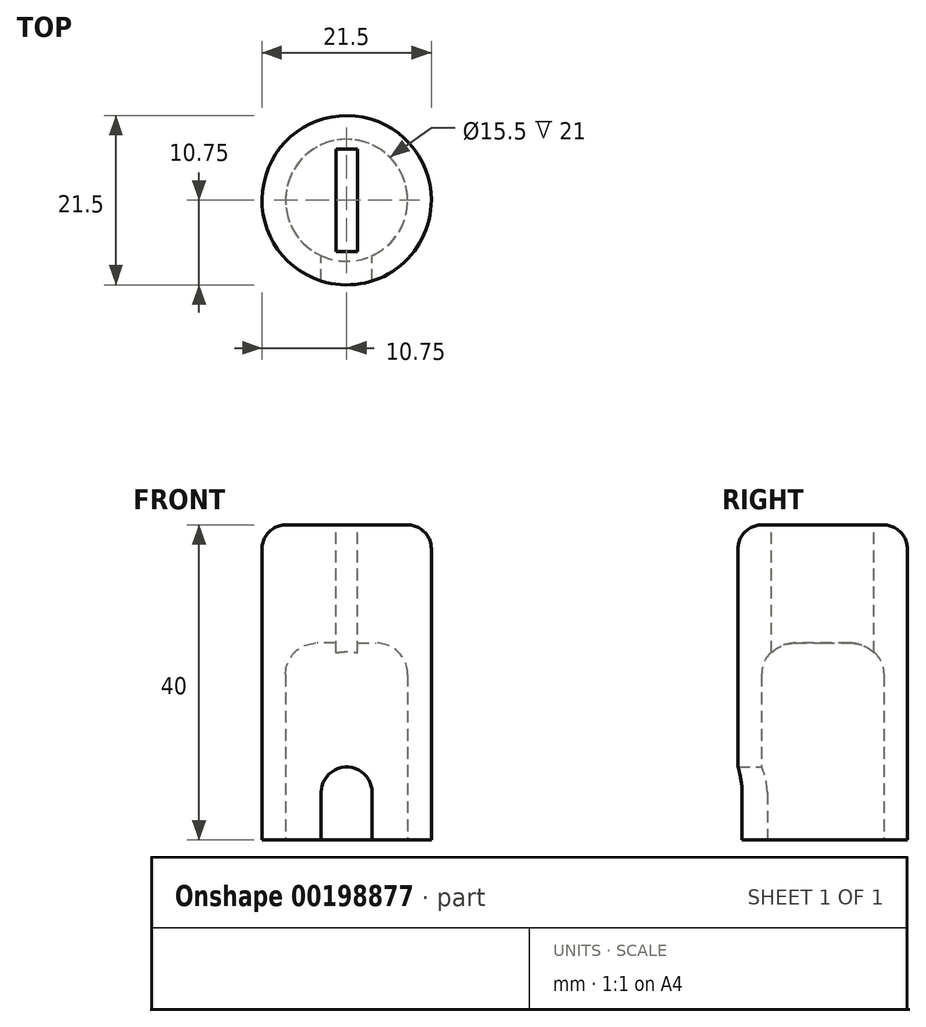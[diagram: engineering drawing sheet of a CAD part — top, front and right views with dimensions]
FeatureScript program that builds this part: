
annotation { "Feature Type Name" : "Feature", "Feature Type Description" : "" }
export const myFeature = defineFeature(function(context is Context, id is Id, definition is map)
    precondition{}
    {
        {
            var Q0;
            Q0=qCreatedBy(makeId("Top.planeOp"),FACE);
            var sketch = newSketch(context, id + "F0", { "sketchPlane" : qUnion([Q0])});
            skCircle(sketch, "E0", {"center": v(0, 0) * mm, "radius": 7.75 * mm});
            skCircle(sketch, "E1", {"center": v(0, 0) * mm, "radius": 10.75 * mm});
            skSolve(sketch);
        }
        {
            var Q0;
            Q0=makeQuery(id+"F0.imprint","IMPRINT",FACE,{"disambiguationData":[TD([[makeQuery(id+"F0.imprint","IMPRINT",EDGE,{"derivedFrom":sQuery(id+"F0.wireOp",EDGE,"E0")}),-1.0]])]});
            var Q1;
            Q1=makeQuery(id+"F0.imprint","IMPRINT",FACE,{"disambiguationData":[TD([[makeQuery(id+"F0.imprint","IMPRINT",EDGE,{"derivedFrom":sQuery(id+"F0.wireOp",EDGE,"E0")}),1.0]])]});
            extrude(context, id + "F1", {"entities" : qUnion([Q0, Q1]), "depth" : 40 * mm});
        }
        {
            var Q0;
            Q0=qCreatedBy(makeId("Front.planeOp"),FACE);
            var sketch = newSketch(context, id + "F2", { "sketchPlane" : qUnion([Q0])});
            skLineSegment(sketch, "E2.bottom", {"start": v(-3.25, 0) * mm, "end": v(3.25, 0) * mm});
            skLineSegment(sketch, "E2.left", {"start": v(-3.25, 0) * mm, "end": v(-3.25, 6) * mm});
            skLineSegment(sketch, "E2.right", {"start": v(3.25, 0) * mm, "end": v(3.25, 6) * mm});
            skArc(sketch, "E3", {"start": v(3.25, 6) * mm, "mid": v(0, 9.25) * mm, "end": v(-3.25, 6) * mm});
            skSolve(sketch);
        }
        {
            var Q0;
            Q0=makeQuery(id+"F2.imprint","IMPRINT",FACE,{"disambiguationData":[TD([[makeQuery(id+"F2.imprint","IMPRINT",EDGE,{"derivedFrom":sQuery(id+"F2.wireOp",EDGE,"E2.bottom")}),1.0]])]});
            extrude(context, id + "F3", {"entities" : qUnion([Q0]), "operationType" : NewBodyOperationType.REMOVE, "depth" : 15 * mm});
        }
        {
            var Q0;
            Q0=makeQuery(id+"F0.imprint","IMPRINT",FACE,{"disambiguationData":[TD([[makeQuery(id+"F0.imprint","IMPRINT",EDGE,{"derivedFrom":sQuery(id+"F0.wireOp",EDGE,"E0")}),1.0]])]});
            var Q1;
            Q1=sQuery(id+"F0.wireOp",EDGE,"E0");
            extrude(context, id + "F4", {"entities" : qUnion([Q0]), "operationType" : NewBodyOperationType.REMOVE, "surfaceEntities" : qUnion([Q1]), "depth" : 25 * mm});
        }
        {
            var Q0;
            Q0=qCreatedBy(makeId("Top.planeOp"),FACE);
            cPlane(context, id + "F5", {"entities" : qUnion([Q0]), "cplaneType" : CPlaneType.OFFSET, "offset" : 40 * mm, "width" : 150 * mm, "height" : 150 * mm});
        }
        {
            var Q0;
            Q0=qCreatedBy(id+"F5.planeOp",FACE);
            var sketch = newSketch(context, id + "F6", { "sketchPlane" : qUnion([Q0])});
            skLineSegment(sketch, "E4.bottom", {"start": v(-1.35, 6.5) * mm, "end": v(1.35, 6.5) * mm});
            skLineSegment(sketch, "E4.top", {"start": v(-1.35, -6.5) * mm, "end": v(1.35, -6.5) * mm});
            skLineSegment(sketch, "E4.left", {"start": v(-1.35, 6.5) * mm, "end": v(-1.35, -6.5) * mm});
            skLineSegment(sketch, "E4.right", {"start": v(1.35, 6.5) * mm, "end": v(1.35, -6.5) * mm});
            skSolve(sketch);
        }
        {
            var Q0;
            Q0=makeQuery(id+"F1.opExtrude","CAP_EDGE",EDGE,{"disambiguationData":[OSD([sQuery(id+"F0.wireOp",EDGE,"E1")])],"isStart":false});
            fillet(context, id + "F7", {"entities" : qUnion([Q0]), "radius" : 3 * mm, "tangentPropagation" : true, "allowEdgeOverflow" : false});
        }
        {
            var Q0;
            Q0 = qSketchRegion(id + "F6", true);
            extrude(context, id + "F8", {"entities" : qUnion([Q0]), "operationType" : NewBodyOperationType.REMOVE, "oppositeDirection" : true, "depth" : 25 * mm});
        }
        {
            var Q0;
            Q0=makeQuery(id+"F4.boolean.opBoolean","COPY",EDGE,{"derivedFrom":makeQuery(id+"F4.opExtrude","CAP_EDGE",EDGE,{"disambiguationData":[OSD([sQuery(id+"F0.wireOp",EDGE,"E0")])],"isStart":false})});
            fillet(context, id + "F9", {"entities" : qUnion([Q0]), "radius" : 4 * mm, "tangentPropagation" : true, "allowEdgeOverflow" : false});
        }
    });
